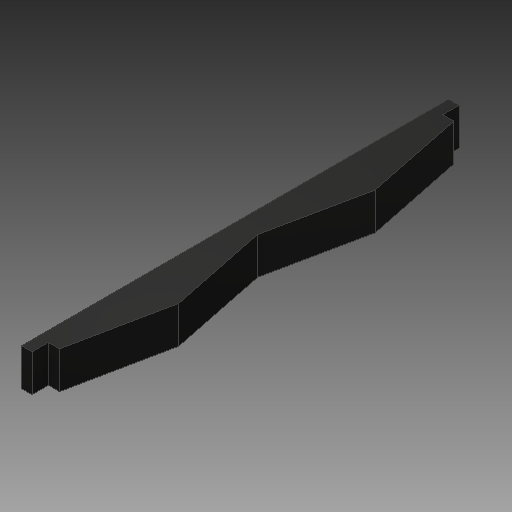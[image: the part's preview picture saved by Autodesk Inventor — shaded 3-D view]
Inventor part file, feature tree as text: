
AUTODESK INVENTOR PART (.ipt)
format: ipt  version: 2017 (Build 210142000, 142)  size: 105,984 bytes
history: native  units: in
note: dims shown in document units (in); Inventor stores cm internally (conversion verified against a paired STEP export)
features: extrude x3, sketch x3
ambient origin geometry x8: Origin, YZ Plane, XZ Plane, XY Plane, X Axis, Y Axis, Z Axis, Center Point
bodies: Solid1 (feature_tree)
feature tree (6):
  extrude  "Extrusion1"  Depth=0.134in
  sketch  "Sketch2"  dims[d2=0.134in d3=0.6115in]
  extrude  "Extrusion2"  Depth=0.134in
  extrude  "Extrusion3"  Depth=0.101in
  sketch  "Sketch1"  dims[d0=2.436in d1=0.134in]
  sketch  "Sketch3"  dims[d4=1.223in d5=0.6115in d6=0.125in d7=0.125in d8=0.229in d9=0.0in d10=0.065in d11=0.065in d12=0.101in d13=0.0in d14=0.101in d15=0.0in]
